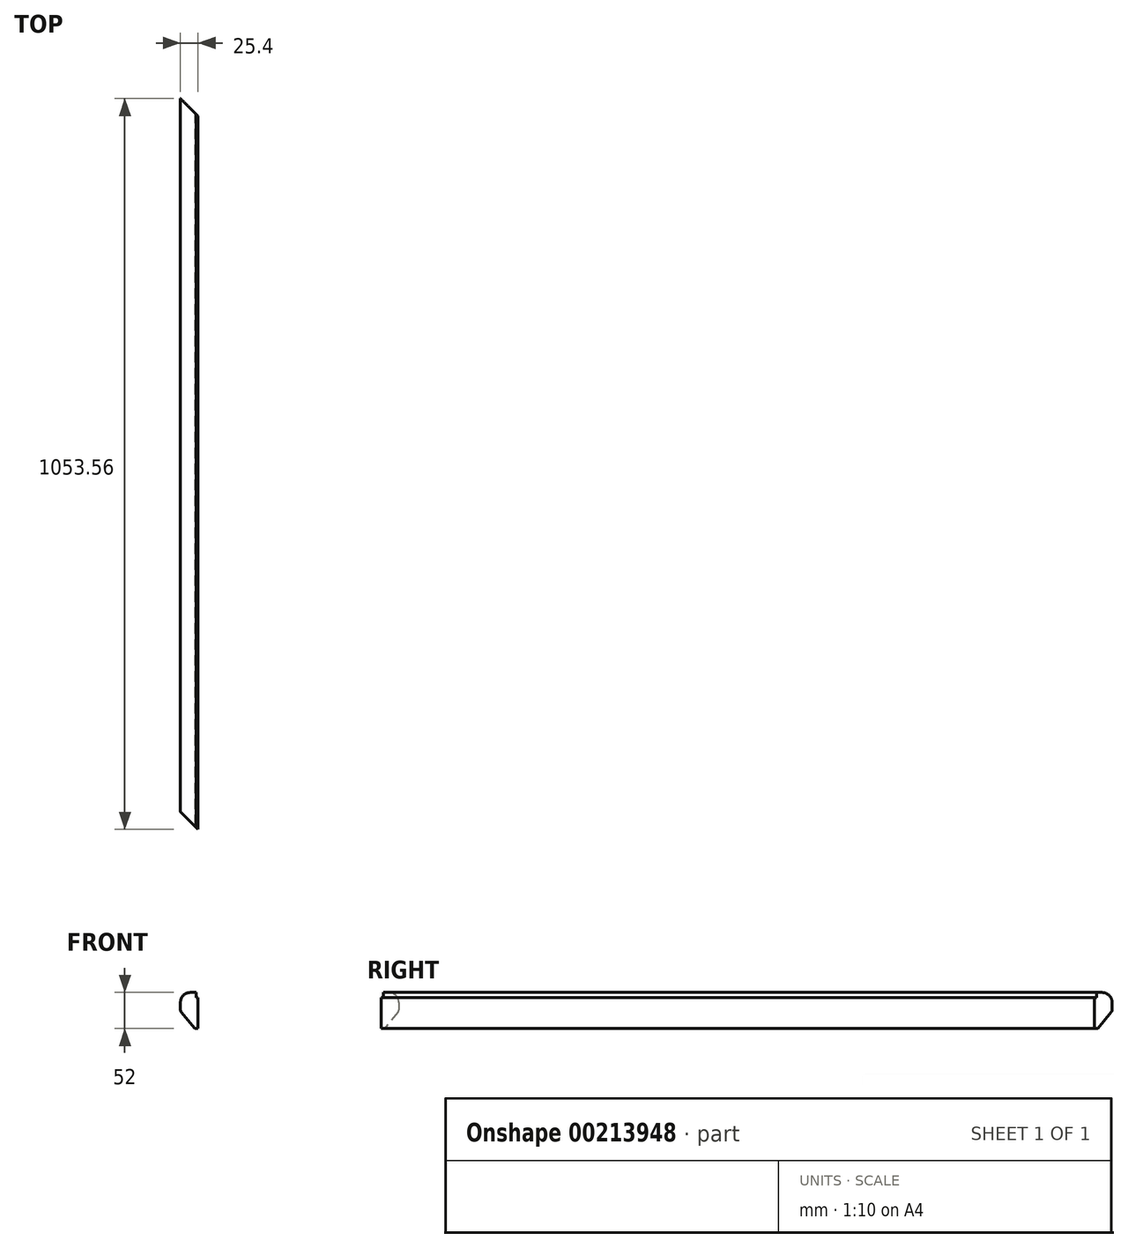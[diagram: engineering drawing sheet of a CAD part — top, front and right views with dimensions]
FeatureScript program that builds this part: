
annotation { "Feature Type Name" : "Feature", "Feature Type Description" : "" }
export const myFeature = defineFeature(function(context is Context, id is Id, definition is map)
    precondition{}
    {
        {
            var Q0;
            Q0=qCreatedBy(makeId("Front.planeOp"),FACE);
            var sketch = newSketch(context, id + "F0", { "sketchPlane" : qUnion([Q0])});
            skLineSegment(sketch, "E0.bottom", {"start": v(-11.4, 0) * mm, "end": v(-3, 0) * mm});
            skLineSegment(sketch, "E0.top", {"start": v(-5, -52) * mm, "end": v(0, -52) * mm});
            skLineSegment(sketch, "E0.left", {"start": v(-25.4, -14) * mm, "end": v(-25.4, -25.22) * mm});
            skLineSegment(sketch, "E0.right", {"start": v(0, -7) * mm, "end": v(0, -52) * mm});
            skLineSegment(sketch, "E1", {"start": v(-24.28, -28.38) * mm, "end": v(-5, -52) * mm});
            skPoint(sketch, "E2.visualSharp", {"position": v(-25.4, 0) * mm});
            skArc(sketch, "E2.filletArc", {"start": v(-11.4, 0) * mm, "mid": v(-21.3, -4.1) * mm, "end": v(-25.4, -14) * mm});
            skPoint(sketch, "E3.visualSharp", {"position": v(-25.4, -27) * mm});
            skArc(sketch, "E3.filletArc", {"start": v(-25.4, -25.22) * mm, "mid": v(-25.11, -26.9) * mm, "end": v(-24.28, -28.38) * mm});
            skLineSegment(sketch, "E4.top", {"start": v(0, -7) * mm, "end": v(-3, -7) * mm});
            skLineSegment(sketch, "E4.right", {"start": v(-3, 0) * mm, "end": v(-3, -7) * mm});
            skPoint(sketch, "E5.orphan", {"position": v(0, 0) * mm});
            skSolve(sketch);
        }
        {
            var Q0;
            Q0 = qSketchRegion(id + "F0", true);
            extrude(context, id + "F1", {"entities" : qUnion([Q0]), "oppositeDirection" : true, "depth" : 1100 * mm});
        }
        {
            var Q0;
            Q0=makeQuery(id+"F1.opExtrude","SWEPT_FACE",FACE,{"disambiguationData":[OSD([sQuery(id+"F0.wireOp",EDGE,"E0.bottom")])]});
            var sketch = newSketch(context, id + "F2", { "sketchPlane" : qUnion([Q0])});
            skLineSegment(sketch, "E6", {"start": v(0, 0) * mm, "end": v(-31.73, 31.73) * mm});
            skLineSegment(sketch, "E7", {"start": v(-31.73, 31.73) * mm, "end": v(-31.73, -13.83) * mm});
            skLineSegment(sketch, "E8", {"start": v(-31.73, -13.83) * mm, "end": v(0, -13.83) * mm});
            skLineSegment(sketch, "E9", {"start": v(0, -13.83) * mm, "end": v(0, 0) * mm});
            skLineSegment(sketch, "E10", {"start": v(0, 1028.16) * mm, "end": v(-42.5, 1070.65) * mm});
            skLineSegment(sketch, "E11", {"start": v(-42.5, 1070.65) * mm, "end": v(-42.5, 1341.93) * mm});
            skLineSegment(sketch, "E12", {"start": v(-42.5, 1341.93) * mm, "end": v(8.04, 1341.93) * mm});
            skLineSegment(sketch, "E13", {"start": v(8.04, 1341.93) * mm, "end": v(8.04, 1032.03) * mm});
            skLineSegment(sketch, "E14", {"start": v(8.04, 1032.03) * mm, "end": v(0, 1028.16) * mm});
            skSolve(sketch);
        }
        {
            var Q0;
            Q0 = qSketchRegion(id + "F2", true);
            extrude(context, id + "F3", {"entities" : qUnion([Q0]), "operationType" : NewBodyOperationType.REMOVE, "endBound" : BoundingType.THROUGH_ALL, "oppositeDirection" : true, "depth" : 25 * mm});
        }
    });
